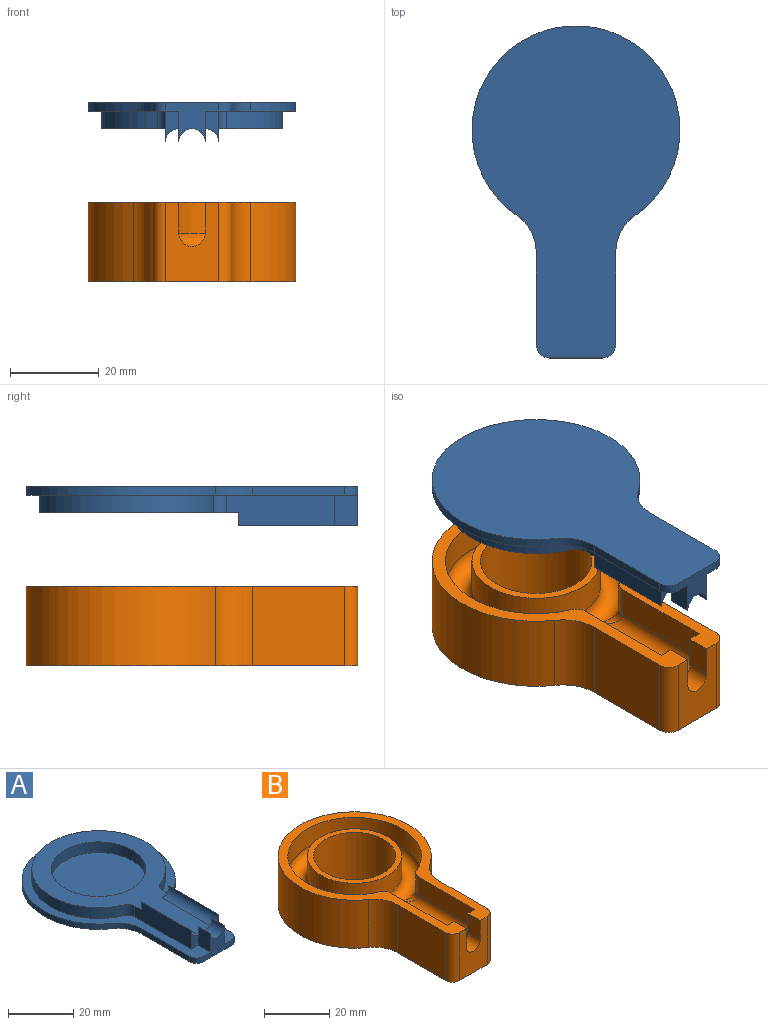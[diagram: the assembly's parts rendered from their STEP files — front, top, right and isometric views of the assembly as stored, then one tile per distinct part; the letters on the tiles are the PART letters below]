
ASSEMBLY  parts=2 mates=1
PART A: 29 faces, bbox 47x75x9 mm
  f0: plane 7x5.38mm, normal (-1,0,0), area 37.5mm2, adj f3,f4,f5,f6,f16,f26
  f1: plane 7x5.38mm, normal (1,0,0), area 37.5mm2, adj f3,f4,f5,f6,f11,f25
  f2: plane 3x3mm, normal (0,1,0), area 1.9mm2, adj f5,f14,f27
  f3: cylinder r=3mm len=6mm, axis (0,-1,0), area 50.4mm2, adj f0,f1,f4,f25,f26
  f4: plane 12x9mm, normal (0,-1,0), area 51.9mm2, adj f0,f1,f3,f6,f10,f18,f19
  f5: plane 66.66x41mm, normal (0,0,1), area 843.1mm2, adj f0,f1,f2,f12,f13,f14,f15,f22
  f6: plane 75x47mm, normal (0,0,1), area 590.8mm2, adj f0,f1,f4,f7,f8,f9,f11,f12
  f7: plane 20.91x2mm, normal (1,0,0), area 41.8mm2, adj f6,f10,f18,f20
  f8: cylinder r=23.5mm len=47mm, axis (0,0,1), area 238.6mm2, adj f6,f10,f20,f21
  f9: plane 20.91x2mm, normal (-1,0,0), area 41.8mm2, adj f6,f10,f19,f21
  f10: plane 75x47mm, normal (0,0,-1), area 2255.9mm2, adj f4,f7,f8,f9,f18,f19,f20,f21
  f11: plane 7x3mm, normal (0,-1,0), area 13.9mm2, adj f1,f6,f12,f28
  f12: plane 24.42x7mm, normal (1,0,0), area 162.4mm2, adj f5,f6,f11,f22,f24,f28
  f13: cylinder r=20.5mm len=41mm, axis (0,0,-1), area 450.8mm2, adj f5,f6,f22,f23
  f14: plane 24.42x7mm, normal (-1,0,0), area 162.4mm2, adj f2,f5,f6,f16,f23,f27
  f15: cylinder r=14.5mm len=29mm, axis (0,0,-1), area 364.4mm2, adj f5,f17
  f16: plane 7x3mm, normal (0,-1,0), area 13.9mm2, adj f0,f6,f14,f27
  f17: plane 29x29mm, normal (0,0,1), area 660.5mm2, adj f15
  f18: cylinder r=3mm len=3mm, axis (0,0,-1), area 9.4mm2, adj f4,f6,f7,f10
  f19: cylinder r=3mm len=3mm, axis (0,0,1), area 9.4mm2, adj f4,f6,f9,f10
  f20: cylinder r=10mm len=8.24mm, axis (0,0,1), area 19.4mm2, adj f6,f7,f8,f10
  f21: cylinder r=10mm len=8.24mm, axis (0,0,1), area 19.4mm2, adj f6,f8,f9,f10
  f22: cylinder r=3mm len=4mm, axis (0,0,-1), area 14.1mm2, adj f5,f6,f12,f13
  f23: cylinder r=3mm len=4mm, axis (0,0,-1), area 14.1mm2, adj f5,f6,f13,f14
  f24: plane 3x3mm, normal (0,1,0), area 1.9mm2, adj f5,f12,f28
  f25: plane 3x3mm, normal (0,1,0), area 1.9mm2, adj f1,f3,f5
  f26: plane 3x3mm, normal (0,1,0), area 1.9mm2, adj f0,f3,f5
  f27: cylinder r=3mm len=21.57mm, axis (0,1,0), area 101.6mm2, adj f2,f5,f14,f16
  f28: cylinder r=3mm len=21.57mm, axis (0,1,0), area 101.6mm2, adj f5,f11,f12,f24
PART B: 29 faces, bbox 47x75x18 mm
  f0: plane 75x47mm, normal (0,0,1), area 590.8mm2, adj f2,f3,f4,f5,f8,f9,f10,f11
  f1: plane 29x29mm, normal (0,0,1), area 161.8mm2, adj f7,f14
  f2: plane 18x12mm, normal (0,-1,0), area 159.9mm2, adj f0,f6,f8,f9,f20,f25,f26
  f3: plane 20.91x18mm, normal (1,0,0), area 376.4mm2, adj f0,f6,f25,f27
  f4: cylinder r=23.5mm len=47mm, axis (0,0,1), area 2147.6mm2, adj f0,f6,f27,f28
  f5: plane 20.91x18mm, normal (-1,0,0), area 376.4mm2, adj f0,f6,f26,f28
  f6: plane 75x47mm, normal (0,0,-1), area 1757.1mm2, adj f2,f3,f4,f5,f7,f25,f26,f27
  f7: cylinder r=12.6mm len=25.2mm, axis (0,0,1), area 1425mm2, adj f1,f6
  f8: plane 7x5.38mm, normal (1,0,0), area 37.6mm2, adj f0,f2,f15,f20
  f9: plane 7x5.38mm, normal (-1,0,0), area 37.6mm2, adj f0,f2,f10,f20
  f10: plane 10x6mm, normal (0,1,0), area 30mm2, adj f0,f9,f11,f16,f18,f20
  f11: plane 24.42x7mm, normal (-1,0,0), area 170.9mm2, adj f0,f10,f18,f21
  f12: cylinder r=20.5mm len=41mm, axis (0,0,1), area 788.8mm2, adj f0,f19,f21,f23
  f13: plane 24.42x7mm, normal (1,0,0), area 170.9mm2, adj f0,f15,f17,f23
  f14: cylinder r=14.5mm len=29mm, axis (0,0,1), area 637.7mm2, adj f1,f19
  f15: plane 10x6mm, normal (0,1,0), area 30mm2, adj f0,f8,f13,f16,f17,f20
  f16: plane 28.88x6mm, normal (0,0,1), area 172.3mm2, adj f10,f15,f17,f18,f19
  f17: cylinder r=3mm len=28.88mm, axis (0,-1,0), area 122.4mm2, adj f13,f15,f16,f24
  f18: cylinder r=3mm len=28.88mm, axis (0,1,0), area 122.4mm2, adj f10,f11,f16,f22
  f19: torus R=17.5mm, axis (0,0,1), area 977.1mm2, adj f12,f14,f16,f22,f24
  f20: cylinder r=3mm len=6mm, axis (0,-1,0), area 50.7mm2, adj f2,f8,f9,f10,f15
  f21: cylinder r=3mm len=7mm, axis (0,0,1), area 24.7mm2, adj f0,f11,f12,f22
  f22: bspline ~4.86x4.47mm, area 12.2mm2, adj f18,f19,f21
  f23: cylinder r=3mm len=7mm, axis (0,0,1), area 24.7mm2, adj f0,f12,f13,f24
  f24: bspline ~4.86x4.47mm, area 12.2mm2, adj f17,f19,f23
  f25: cylinder r=3mm len=18mm, axis (0,0,-1), area 84.8mm2, adj f0,f2,f3,f6
  f26: cylinder r=3mm len=18mm, axis (0,0,1), area 84.8mm2, adj f0,f2,f5,f6
  f27: cylinder r=10mm len=18mm, axis (0,0,1), area 174.2mm2, adj f0,f3,f4,f6
  f28: cylinder r=10mm len=18mm, axis (0,0,1), area 174.2mm2, adj f0,f4,f5,f6
PLACE A rot(axis=(0,1,0),180deg) t=(28.81,18.25,23.03)mm
PLACE B t=(28.81,18.25,2.42)mm fixed
MATE slider A.f13 <-> B.f7  axis (0,0,1) through (28.81,18.25,21.03)mm
